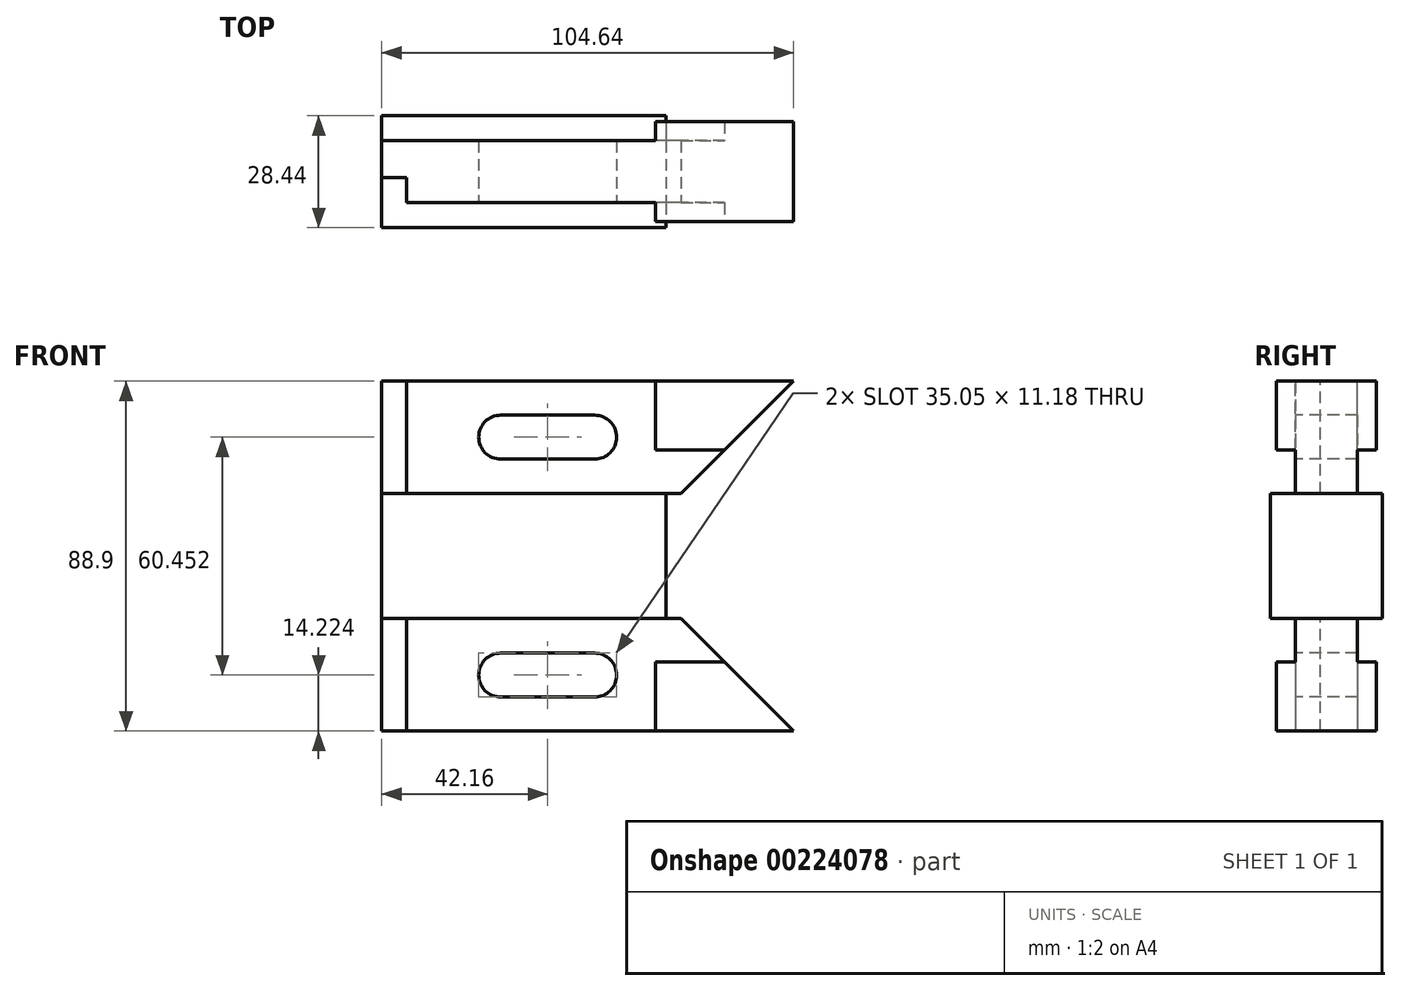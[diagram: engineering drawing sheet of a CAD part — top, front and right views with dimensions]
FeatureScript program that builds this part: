
annotation { "Feature Type Name" : "Feature", "Feature Type Description" : "" }
export const myFeature = defineFeature(function(context is Context, id is Id, definition is map)
    precondition{}
    {
        {
            var Q0;
            Q0=qCreatedBy(makeId("Right.planeOp"),FACE);
            var sketch = newSketch(context, id + "F0", { "sketchPlane" : qUnion([Q0])});
            skLineSegment(sketch, "E0.bottom", {"start": v(-14.22, 15.88) * mm, "end": v(14.22, 15.88) * mm});
            skLineSegment(sketch, "E0.top", {"start": v(-14.22, -15.88) * mm, "end": v(14.22, -15.88) * mm});
            skLineSegment(sketch, "E0.left", {"start": v(-14.22, 15.88) * mm, "end": v(-14.22, -15.88) * mm});
            skLineSegment(sketch, "E0.right", {"start": v(14.22, 15.88) * mm, "end": v(14.22, -15.88) * mm});
            skPoint(sketch, "E0.middle", {"position": v(0, 0) * mm});
            skLineSegment(sketch, "E1", {"start": v(-7.87, 15.88) * mm, "end": v(-7.87, 26.92) * mm});
            skLineSegment(sketch, "E2", {"start": v(-7.87, 26.92) * mm, "end": v(-12.7, 26.92) * mm});
            skLineSegment(sketch, "E3", {"start": v(-12.7, 26.92) * mm, "end": v(-12.7, 44.45) * mm});
            skLineSegment(sketch, "E4", {"start": v(-12.7, 44.45) * mm, "end": v(12.7, 44.45) * mm});
            skLineSegment(sketch, "E5", {"start": v(7.87, 15.88) * mm, "end": v(7.87, 26.92) * mm});
            skLineSegment(sketch, "E6", {"start": v(7.87, 26.92) * mm, "end": v(12.7, 26.92) * mm});
            skLineSegment(sketch, "E7", {"start": v(12.7, 26.92) * mm, "end": v(12.7, 44.45) * mm});
            skLineSegment(sketch, "E8", {"start": v(-71.52, 0) * mm, "end": v(87.9, 0) * mm, "construction": true});
            skLineSegment(sketch, "E9.MirrorCS", {"start": v(-12.7, -44.45) * mm, "end": v(12.7, -44.45) * mm});
            skLineSegment(sketch, "E10.MirrorCS", {"start": v(-12.7, -26.92) * mm, "end": v(-12.7, -44.45) * mm});
            skLineSegment(sketch, "E11.MirrorCS", {"start": v(12.7, -26.92) * mm, "end": v(12.7, -44.45) * mm});
            skLineSegment(sketch, "E12.MirrorCS", {"start": v(7.87, -15.88) * mm, "end": v(7.87, -26.92) * mm});
            skLineSegment(sketch, "E13.MirrorCS", {"start": v(-7.87, -15.88) * mm, "end": v(-7.87, -26.92) * mm});
            skLineSegment(sketch, "E14.MirrorCS", {"start": v(7.87, -26.92) * mm, "end": v(12.7, -26.92) * mm});
            skLineSegment(sketch, "E15.MirrorCS", {"start": v(-7.87, -26.92) * mm, "end": v(-12.7, -26.92) * mm});
            skSolve(sketch);
        }
        {
            var Q0;
            {var subQ0=sQuery(id+"F0.wireOp",EDGE,"E1");Q0=makeQuery(id+"F0.imprint","IMPRINT",FACE,{"disambiguationData":[TD([[makeQuery(id+"F0.imprint","IMPRINT",EDGE,{"derivedFrom":subQ0}),-1.0]])]});}
            var Q1;
            {var subQ0=sQuery(id+"F0.wireOp",EDGE,"E0.left");Q1=makeQuery(id+"F0.imprint","IMPRINT",FACE,{"disambiguationData":[TD([[makeQuery(id+"F0.imprint","IMPRINT",EDGE,{"derivedFrom":subQ0}),1.0]])]});}
            var Q2;
            Q2=makeQuery(id+"F0.imprint","IMPRINT",FACE,{"disambiguationData":[TD([[makeQuery(id+"F0.imprint","IMPRINT",EDGE,{"derivedFrom":sQuery(id+"F0.wireOp",EDGE,"E9.MirrorCS")}),1.0]])]});
            extrude(context, id + "F1", {"entities" : qUnion([Q0, Q1, Q2]), "endBound" : BoundingType.SYMMETRIC, "depth" : 104.65 * mm});
        }
        {
            var Q0;
            Q0=makeQuery(id+"F1.opExtrude","SWEPT_FACE",FACE,{"disambiguationData":[OSD([sQuery(id+"F0.wireOp",EDGE,"E3")])]});
            var sketch = newSketch(context, id + "F2", { "sketchPlane" : qUnion([Q0])});
            skLineSegment(sketch, "E16", {"start": v(-52.32, 44.45) * mm, "end": v(-52.32, 15.88) * mm});
            skLineSegment(sketch, "E17", {"start": v(-52.32, 44.45) * mm, "end": v(-45.97, 44.45) * mm});
            skLineSegment(sketch, "E18", {"start": v(-45.97, 44.45) * mm, "end": v(-45.97, 15.88) * mm});
            skLineSegment(sketch, "E19", {"start": v(-45.97, 15.88) * mm, "end": v(-52.32, 15.88) * mm});
            skLineSegment(sketch, "E20", {"start": v(-105.2, 0) * mm, "end": v(117.4, 0) * mm, "construction": true});
            skLineSegment(sketch, "E21", {"start": v(-118.75, 30.23) * mm, "end": v(110.7, 30.23) * mm, "construction": true});
            skArc(sketch, "E22", {"start": v(-22.1, 35.81) * mm, "mid": v(-27.69, 30.23) * mm, "end": v(-22.1, 24.64) * mm});
            skArc(sketch, "E23", {"start": v(1.78, 24.64) * mm, "mid": v(7.37, 30.23) * mm, "end": v(1.78, 35.81) * mm});
            skLineSegment(sketch, "E24", {"start": v(-22.1, 35.81) * mm, "end": v(1.78, 35.81) * mm});
            skLineSegment(sketch, "E25", {"start": v(-22.1, 24.64) * mm, "end": v(1.78, 24.64) * mm});
            skLineSegment(sketch, "E26.MirrorCS", {"start": v(-22.1, -35.81) * mm, "end": v(1.78, -35.81) * mm});
            skLineSegment(sketch, "E27.MirrorCS", {"start": v(-22.1, -24.64) * mm, "end": v(1.78, -24.64) * mm});
            skArc(sketch, "E28.MirrorCS", {"start": v(1.78, -24.64) * mm, "mid": v(7.37, -30.23) * mm, "end": v(1.78, -35.81) * mm});
            skArc(sketch, "E29.MirrorCS", {"start": v(-22.1, -35.81) * mm, "mid": v(-27.69, -30.23) * mm, "end": v(-22.1, -24.64) * mm});
            skLineSegment(sketch, "E30.MirrorCS", {"start": v(-45.97, -44.45) * mm, "end": v(-45.97, -15.88) * mm});
            skLineSegment(sketch, "E31.MirrorCS", {"start": v(-52.32, -44.45) * mm, "end": v(-52.32, -15.88) * mm});
            skLineSegment(sketch, "E32.MirrorCS", {"start": v(-52.32, -44.45) * mm, "end": v(-45.97, -44.45) * mm});
            skLineSegment(sketch, "E33.MirrorCS", {"start": v(-45.97, -15.88) * mm, "end": v(-52.32, -15.88) * mm});
            skSolve(sketch);
        }
        {
            var Q0;
            {var subQ0=sQuery(id+"F2.wireOp",EDGE,"E24");Q0=makeQuery(id+"F2.imprint","IMPRINT",FACE,{"disambiguationData":[TD([[makeQuery(id+"F2.imprint","IMPRINT",EDGE,{"derivedFrom":subQ0}),-1.0]])]});}
            var Q1;
            {var subQ0=sQuery(id+"F2.wireOp",EDGE,"E25");Q1=makeQuery(id+"F2.imprint","IMPRINT",FACE,{"disambiguationData":[TD([[makeQuery(id+"F2.imprint","IMPRINT",EDGE,{"derivedFrom":subQ0}),1.0]])]});}
            var Q2;
            Q2=makeQuery(id+"F2.imprint","IMPRINT",FACE,{"disambiguationData":[TD([[makeQuery(id+"F2.imprint","IMPRINT",EDGE,{"derivedFrom":sQuery(id+"F2.wireOp",EDGE,"E26.MirrorCS")}),1.0]])]});
            extrude(context, id + "F3", {"entities" : qUnion([Q0, Q1, Q2]), "operationType" : NewBodyOperationType.REMOVE, "endBound" : BoundingType.THROUGH_ALL, "oppositeDirection" : true, "depth" : 25.4 * mm});
        }
        {
            var Q0;
            {var subQ4=sQuery(id+"F2.wireOp",EDGE,"E17");Q0=makeQuery(id+"F2.imprint","IMPRINT",FACE,{"disambiguationData":[TD([[makeQuery(id+"F2.imprint","IMPRINT",EDGE,{"derivedFrom":subQ4}),1.0]])]});}
            var Q1;
            Q1=makeQuery(id+"F2.imprint","IMPRINT",FACE,{"disambiguationData":[TD([[makeQuery(id+"F2.imprint","IMPRINT",EDGE,{"derivedFrom":sQuery(id+"F2.wireOp",EDGE,"E30.MirrorCS")}),1.0]])]});
            var Q2;
            {var subQ3=sQuery(id+"F2.wireOp",EDGE,"E19");Q2=makeQuery(id+"F2.imprint","IMPRINT",FACE,{"disambiguationData":[TD([[makeQuery(id+"F2.imprint","IMPRINT",EDGE,{"derivedFrom":subQ3}),-1.0]])]});}
            var Q3;
            Q3=sQuery(id+"F2.wireOp",EDGE,"E18");
            var Q4;
            Q4=sQuery(id+"F2.wireOp",EDGE,"E16");
            var Q5;
            Q5=sQuery(id+"F2.wireOp",EDGE,"E30.MirrorCS");
            var Q6;
            Q6=sQuery(id+"F2.wireOp",EDGE,"E31.MirrorCS");
            var Q7;
            Q7=sQuery(id+"F2.wireOp",EDGE,"E17");
            var Q8;
            Q8=sQuery(id+"F2.wireOp",EDGE,"E19");
            var Q9;
            Q9=sQuery(id+"F2.wireOp",EDGE,"E33.MirrorCS");
            var Q10;
            Q10=sQuery(id+"F2.wireOp",EDGE,"E32.MirrorCS");
            extrude(context, id + "F4", {"entities" : qUnion([Q0, Q1, Q2]), "operationType" : NewBodyOperationType.REMOVE, "surfaceEntities" : qUnion([Q3, Q4, Q5, Q6, Q7, Q8, Q9, Q10]), "oppositeDirection" : true, "depth" : 11.18 * mm});
        }
        {
            var Q0;
            Q0=makeQuery(id+"F1.opExtrude","SWEPT_FACE",FACE,{"disambiguationData":[OSD([sQuery(id+"F0.wireOp",EDGE,"E3")])]});
            var sketch = newSketch(context, id + "F5", { "sketchPlane" : qUnion([Q0])});
            skLineSegment(sketch, "E34", {"start": v(52.32, 44.45) * mm, "end": v(23.75, 15.88) * mm});
            skLineSegment(sketch, "E35", {"start": v(-74.57, 0) * mm, "end": v(80.38, 0) * mm, "construction": true});
            skLineSegment(sketch, "E36", {"start": v(23.75, 15.88) * mm, "end": v(19.94, 15.88) * mm});
            skLineSegment(sketch, "E37", {"start": v(19.94, 15.88) * mm, "end": v(19.94, 0) * mm});
            skLineSegment(sketch, "E38.MirrorCS", {"start": v(52.32, -44.45) * mm, "end": v(23.75, -15.88) * mm});
            skLineSegment(sketch, "E39.MirrorCS", {"start": v(23.75, -15.88) * mm, "end": v(19.94, -15.88) * mm});
            skLineSegment(sketch, "E40.MirrorCS", {"start": v(19.94, -15.88) * mm, "end": v(19.94, 0) * mm});
            skLineSegment(sketch, "E41", {"start": v(52.32, 44.45) * mm, "end": v(52.32, -44.45) * mm});
            skSolve(sketch);
        }
        {
            var Q0;
            Q0 = qSketchRegion(id + "F5", true);
            extrude(context, id + "F6", {"entities" : qUnion([Q0]), "operationType" : NewBodyOperationType.REMOVE, "endBound" : BoundingType.THROUGH_ALL, "oppositeDirection" : true, "depth" : 76.2 * mm});
        }
        {
            var Q0;
            Q0 = qSketchRegion(id + "F5", true);
            extrude(context, id + "F7", {"entities" : qUnion([Q0]), "operationType" : NewBodyOperationType.REMOVE, "endBound" : BoundingType.THROUGH_ALL, "depth" : 25.4 * mm});
        }
        {
            var Q0;
            Q0=makeQuery(id+"F1.opExtrude","SWEPT_FACE",FACE,{"disambiguationData":[OSD([sQuery(id+"F0.wireOp",EDGE,"E0.left")])]});
            var sketch = newSketch(context, id + "F8", { "sketchPlane" : qUnion([Q0])});
            skLineSegment(sketch, "E42.bottom", {"start": v(-52.32, 15.87) * mm, "end": v(17.27, 15.87) * mm});
            skLineSegment(sketch, "E42.top", {"start": v(-52.32, 44.45) * mm, "end": v(17.27, 44.45) * mm});
            skLineSegment(sketch, "E42.left", {"start": v(-52.32, 15.87) * mm, "end": v(-52.32, 44.45) * mm});
            skLineSegment(sketch, "E42.right", {"start": v(17.27, 15.87) * mm, "end": v(17.27, 44.45) * mm});
            skLineSegment(sketch, "E43", {"start": v(-76.29, 0) * mm, "end": v(42.02, 0) * mm, "construction": true});
            skLineSegment(sketch, "E44.MirrorCS", {"start": v(-52.32, -15.87) * mm, "end": v(-52.32, -44.45) * mm});
            skLineSegment(sketch, "E45.MirrorCS", {"start": v(-52.32, -44.45) * mm, "end": v(17.27, -44.45) * mm});
            skLineSegment(sketch, "E46.MirrorCS", {"start": v(-52.32, -15.87) * mm, "end": v(17.27, -15.87) * mm});
            skLineSegment(sketch, "E47.MirrorCS", {"start": v(17.27, -15.87) * mm, "end": v(17.27, -44.45) * mm});
            skSolve(sketch);
        }
        {
            var Q0;
            Q0 = qSketchRegion(id + "F8", true);
            extrude(context, id + "F9", {"entities" : qUnion([Q0]), "operationType" : NewBodyOperationType.REMOVE, "oppositeDirection" : true, "depth" : 6.35 * mm});
        }
        {
            var Q0;
            Q0=makeQuery(id+"F1.opExtrude","SWEPT_FACE",FACE,{"disambiguationData":[OSD([sQuery(id+"F0.wireOp",EDGE,"E0.right")])]});
            var sketch = newSketch(context, id + "F10", { "sketchPlane" : qUnion([Q0])});
            skLineSegment(sketch, "E48.bottom", {"start": v(52.32, 15.88) * mm, "end": v(-17.27, 15.88) * mm});
            skLineSegment(sketch, "E48.top", {"start": v(52.32, 44.45) * mm, "end": v(-17.27, 44.45) * mm});
            skLineSegment(sketch, "E48.left", {"start": v(52.32, 15.88) * mm, "end": v(52.32, 44.45) * mm});
            skLineSegment(sketch, "E48.right", {"start": v(-17.27, 15.88) * mm, "end": v(-17.27, 44.45) * mm});
            skLineSegment(sketch, "E49.MirrorCS", {"start": v(-17.27, -15.87) * mm, "end": v(-17.27, -44.45) * mm});
            skLineSegment(sketch, "E50.MirrorCS", {"start": v(52.32, -15.87) * mm, "end": v(-17.27, -15.87) * mm});
            skLineSegment(sketch, "E51.MirrorCS", {"start": v(52.32, -44.45) * mm, "end": v(-17.27, -44.45) * mm});
            skLineSegment(sketch, "E52.MirrorCS", {"start": v(52.32, -15.87) * mm, "end": v(52.32, -44.45) * mm});
            skSolve(sketch);
        }
        {
            var Q0;
            Q0 = qSketchRegion(id + "F10", true);
            extrude(context, id + "F11", {"entities" : qUnion([Q0]), "operationType" : NewBodyOperationType.REMOVE, "oppositeDirection" : true, "depth" : 6.35 * mm});
        }
    });
